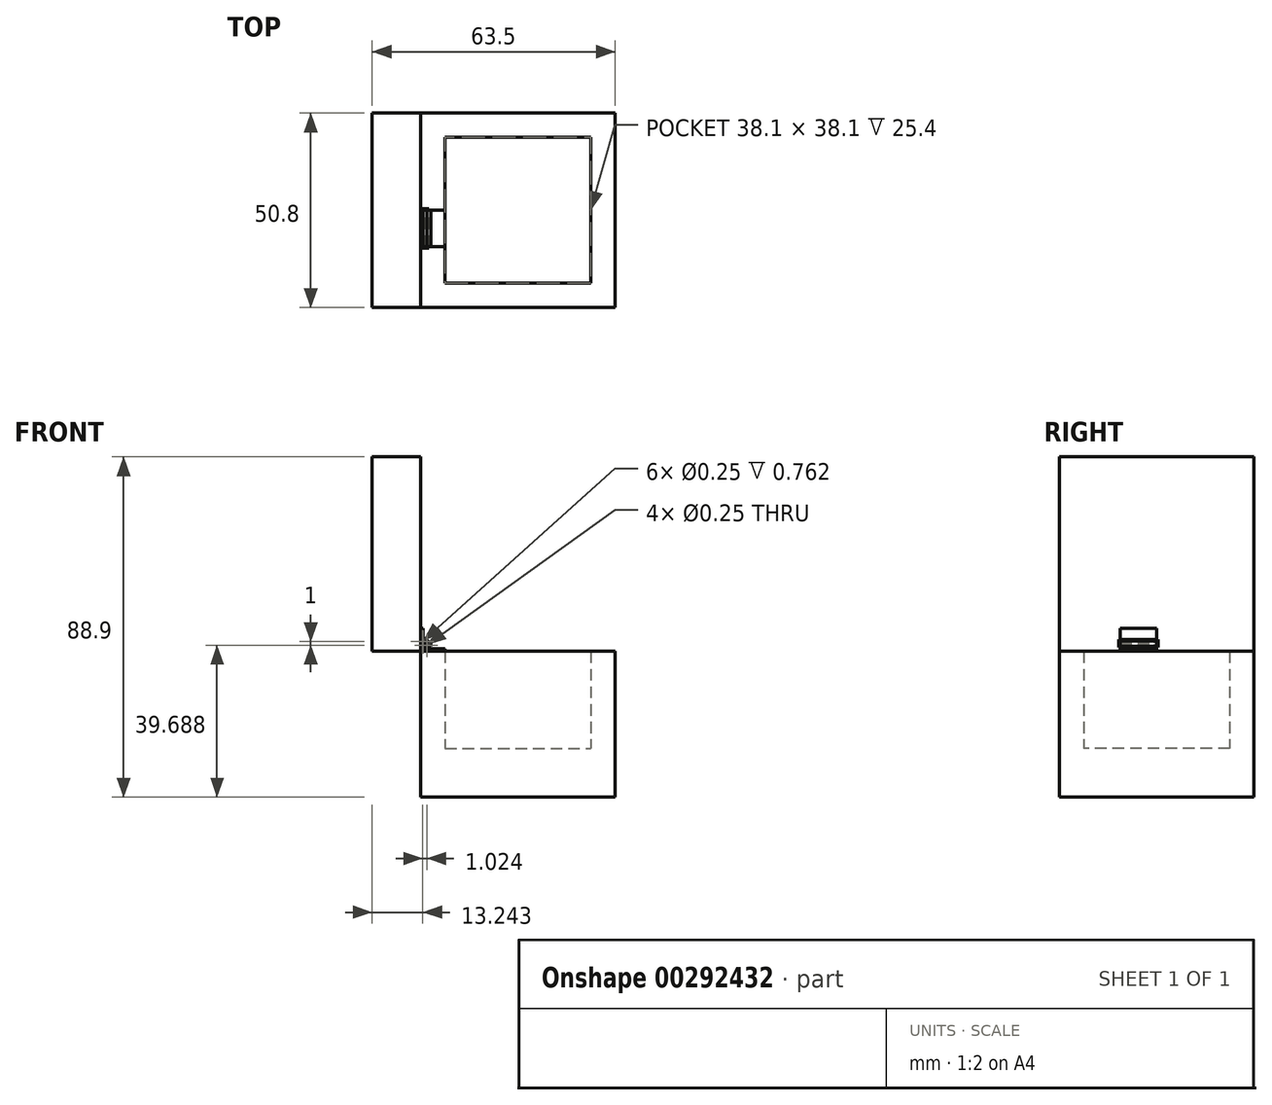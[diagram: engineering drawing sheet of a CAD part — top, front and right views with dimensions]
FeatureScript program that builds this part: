
annotation { "Feature Type Name" : "Feature", "Feature Type Description" : "" }
export const myFeature = defineFeature(function(context is Context, id is Id, definition is map)
    precondition{}
    {
        {
            var Q0;
            Q0=qCreatedBy(makeId("Top.planeOp"),FACE);
            var sketch = newSketch(context, id + "F0", { "sketchPlane" : qUnion([Q0])});
            skLineSegment(sketch, "E0.bottom", {"start": v(0, 25.41) * mm, "end": v(50.8, 25.41) * mm});
            skLineSegment(sketch, "E0.top", {"start": v(0, -25.39) * mm, "end": v(50.8, -25.39) * mm});
            skLineSegment(sketch, "E0.left", {"start": v(0, 25.41) * mm, "end": v(0, -25.39) * mm});
            skLineSegment(sketch, "E0.right", {"start": v(50.8, 25.41) * mm, "end": v(50.8, -25.39) * mm});
            skPoint(sketch, "E0.middle", {"position": v(25.4, 0.01) * mm});
            skLineSegment(sketch, "E1.bottom", {"start": v(6.35, 19.06) * mm, "end": v(44.45, 19.06) * mm});
            skLineSegment(sketch, "E1.top", {"start": v(6.35, -19.04) * mm, "end": v(44.45, -19.04) * mm});
            skLineSegment(sketch, "E1.left", {"start": v(6.35, 19.06) * mm, "end": v(6.35, -19.04) * mm});
            skLineSegment(sketch, "E1.right", {"start": v(44.45, 19.06) * mm, "end": v(44.45, -19.04) * mm});
            skSolve(sketch);
        }
        {
            var Q0;
            Q0=makeQuery(id+"F0.imprint","IMPRINT",FACE,{"disambiguationData":[TD([[makeQuery(id+"F0.imprint","IMPRINT",EDGE,{"derivedFrom":sQuery(id+"F0.wireOp",EDGE,"E0.bottom")}),-1.0]])]});
            extrude(context, id + "F1", {"entities" : qUnion([Q0]), "depth" : 25.4 * mm});
        }
        {
            var Q0;
            Q0=qCreatedBy(makeId("Top.planeOp"),FACE);
            var sketch = newSketch(context, id + "F2", { "sketchPlane" : qUnion([Q0])});
            skLineSegment(sketch, "E2.bottom", {"start": v(50.8, 25.41) * mm, "end": v(0, 25.41) * mm});
            skLineSegment(sketch, "E2.top", {"start": v(50.8, -25.39) * mm, "end": v(0, -25.39) * mm});
            skLineSegment(sketch, "E2.left", {"start": v(50.8, 25.41) * mm, "end": v(50.8, -25.39) * mm});
            skLineSegment(sketch, "E2.right", {"start": v(0, 25.41) * mm, "end": v(0, -25.39) * mm});
            skPoint(sketch, "E2.middle", {"position": v(25.4, 0.01) * mm});
            skSolve(sketch);
        }
        {
            var Q0;
            Q0=makeQuery(id+"F2.imprint","IMPRINT",FACE,{"disambiguationData":[TD([[makeQuery(id+"F2.imprint","IMPRINT",EDGE,{"derivedFrom":sQuery(id+"F2.wireOp",EDGE,"E2.bottom")}),1.0]])]});
            extrude(context, id + "F3", {"entities" : qUnion([Q0]), "operationType" : NewBodyOperationType.ADD, "oppositeDirection" : true, "depth" : 12.7 * mm});
        }
        {
            var Q0;
            Q0=qCreatedBy(makeId("Right.planeOp"),FACE);
            var sketch = newSketch(context, id + "F4", { "sketchPlane" : qUnion([Q0])});
            skLineSegment(sketch, "E3.bottom", {"start": v(25.41, 25.4) * mm, "end": v(-25.39, 25.4) * mm});
            skLineSegment(sketch, "E3.top", {"start": v(25.41, 38.1) * mm, "end": v(-25.39, 38.1) * mm});
            skLineSegment(sketch, "E3.left", {"start": v(25.41, 25.4) * mm, "end": v(25.41, 38.1) * mm});
            skLineSegment(sketch, "E3.right", {"start": v(-25.39, 25.4) * mm, "end": v(-25.39, 38.1) * mm});
            skSolve(sketch);
        }
        {
            var Q0;
            Q0=qSketchRegion(id+"F4",true);
            extrude(context, id + "F5", {"entities" : qUnion([Q0]), "depth" : 50.8 * mm});
        }
        {
            var Q0;
            Q0=makeQuery(id+"F5.opExtrude","SWEPT_BODY",BODY,{"disambiguationData":[OSD([sQuery(id+"F4.wireOp",EDGE,"E3.bottom"),sQuery(id+"F4.wireOp",EDGE,"E3.top"),sQuery(id+"F4.wireOp",EDGE,"E3.left"),sQuery(id+"F4.wireOp",EDGE,"E3.right")])]});
            var Q1;
            Q1=makeQuery(id+"F5.opExtrude","CAP_EDGE",EDGE,{"disambiguationData":[OSD([sQuery(id+"F4.wireOp",EDGE,"E3.bottom")])],"isStart":true});
            transform(context, id + "F6", {"entities" : qUnion([Q0]), "transformType" : TransformType.ROTATION, "transformAxis" : qUnion([Q1]), "angle" : 90 * degree, "makeCopy" : false});
        }
        {
            var Q0;
            Q0=qCreatedBy(makeId("Front.planeOp"),FACE);
            var sketch = newSketch(context, id + "F7", { "sketchPlane" : qUnion([Q0])});
            skLineSegment(sketch, "E4.bottom", {"start": v(6.35, 26.04) * mm, "end": v(2.54, 26.04) * mm});
            skLineSegment(sketch, "E4.top", {"start": v(6.35, 25.4) * mm, "end": v(2.54, 25.4) * mm});
            skLineSegment(sketch, "E4.left", {"start": v(6.35, 26.04) * mm, "end": v(6.35, 25.4) * mm});
            skLineSegment(sketch, "E5", {"start": v(2.54, 26.04) * mm, "end": v(2.54, 25.4) * mm});
            skPoint(sketch, "E6", {"position": v(2.54, 26.04) * mm});
            skLineSegment(sketch, "E7", {"start": v(2.54, 26.04) * mm, "end": v(1.59, 26.48) * mm});
            skArc(sketch, "E8", {"start": v(2.07, 27.09) * mm, "mid": v(1.17, 27.3) * mm, "end": v(1.59, 26.48) * mm});
            skPoint(sketch, "E9", {"position": v(1.56, 25.85) * mm});
            skLineSegment(sketch, "E10", {"start": v(2.54, 25.4) * mm, "end": v(1.56, 25.85) * mm});
            skArc(sketch, "E11", {"start": v(2.7, 26.99) * mm, "mid": v(0.77, 27.8) * mm, "end": v(1.56, 25.85) * mm});
            skLineSegment(sketch, "E12", {"start": v(2.7, 26.99) * mm, "end": v(2.7, 26.76) * mm});
            skLineSegment(sketch, "E13", {"start": v(2.07, 27.09) * mm, "end": v(2.09, 26.98) * mm});
            skLineSegment(sketch, "E14", {"start": v(2.7, 26.76) * mm, "end": v(2.09, 26.98) * mm});
            skPoint(sketch, "E15", {"position": v(6.35, 25.4) * mm});
            skPoint(sketch, "E16", {"position": v(6.35, 26.04) * mm});
            skSolve(sketch);
        }
        {
            var Q0;
            {var subQ2=sQuery(id+"F7.wireOp",EDGE,"49d8aea8-701a-44cc-aa5f-3c914806f390");Q0=makeQuery(id+"F7.imprint","IMPRINT",FACE,{"disambiguationData":[TD([[makeQuery(id+"F7.imprint","IMPRINT",EDGE,{"derivedFrom":subQ2}),1.0]])]});}
            var Q1;
            Q1=makeQuery(id+"F7.imprint","IMPRINT",FACE,{"disambiguationData":[TD([[makeQuery(id+"F7.imprint","IMPRINT",EDGE,{"derivedFrom":sQuery(id+"F7.wireOp",EDGE,"453310b4-ccfe-4605-a67d-a863b6ff2596")}),-1.0]])]});
            var Q2;
            Q2=makeQuery(id+"F7.imprint","IMPRINT",FACE,{"disambiguationData":[TD([[makeQuery(id+"F7.imprint","IMPRINT",EDGE,{"derivedFrom":sQuery(id+"F7.wireOp",EDGE,"E4.bottom")}),1.0]])]});
            extrude(context, id + "F8", {"entities" : qUnion([Q0, Q1, Q2]), "operationType" : NewBodyOperationType.ADD, "depth" : 9.52 * mm});
        }
        {
            var Q0;
            Q0=qCreatedBy(makeId("Front.planeOp"),FACE);
            var sketch = newSketch(context, id + "F9", { "sketchPlane" : qUnion([Q0])});
            skPoint(sketch, "E17", {"position": v(1.57, 28.12) * mm});
            skPoint(sketch, "E18", {"position": v(0.96, 27.94) * mm});
            skPoint(sketch, "E19", {"position": v(0.64, 28.5) * mm});
            skLineSegment(sketch, "E20", {"start": v(0, 28.27) * mm, "end": v(0, 27.63) * mm});
            skPoint(sketch, "E21.MirrorP", {"position": v(0.64, 27.63) * mm});
            skLineSegment(sketch, "E22.MirrorCS", {"start": v(0.64, 31.44) * mm, "end": v(0, 31.44) * mm});
            skLineSegment(sketch, "E23", {"start": v(0, 31.44) * mm, "end": v(0, 28.27) * mm});
            skPoint(sketch, "E24", {"position": v(0.8, 27.82) * mm});
            skLineSegment(sketch, "E25", {"start": v(0.64, 31.44) * mm, "end": v(0.64, 28.5) * mm});
            skLineSegment(sketch, "E26", {"start": v(1.57, 28.12) * mm, "end": v(1.57, 28.5) * mm});
            skLineSegment(sketch, "E27", {"start": v(1.57, 28.5) * mm, "end": v(0.64, 28.5) * mm});
            skArc(sketch, "E28", {"start": v(1.57, 28.12) * mm, "mid": v(1.04, 28) * mm, "end": v(0.64, 27.63) * mm});
            skPoint(sketch, "E29", {"position": v(1.57, 26.99) * mm});
            skCircle(sketch, "E30", {"center": v(1.57, 26.99) * mm, "radius": 0.5 * mm});
            skPoint(sketch, "E31", {"position": v(0.5, 27.37) * mm});
            skArc(sketch, "E32", {"start": v(0.64, 27.63) * mm, "mid": v(0.48, 27.33) * mm, "end": v(0.43, 26.99) * mm});
            skLineSegment(sketch, "E33", {"start": v(0.43, 26.99) * mm, "end": v(0, 26.99) * mm});
            skLineSegment(sketch, "E34", {"start": v(0, 27.63) * mm, "end": v(0, 26.99) * mm});
            skSolve(sketch);
        }
        {
            var Q0;
            Q0=qSketchRegion(id+"F7",true);
            extrude(context, id + "F10", {"entities" : qUnion([Q0]), "operationType" : NewBodyOperationType.ADD, "depth" : 9.52 * mm});
        }
        {
            var Q0;
            {var subQ0=sQuery(id+"F9.wireOp",EDGE,"E30");var subQ1=makeQuery(id+"F9.imprint","INTERSECT",VERTEX,{"derivedFrom":[subQ0,sQuery(id+"F9.wireOp",EDGE,"qVxJkQmu-DeZt-bHWC-hwNS-qI8DtV47FeaQ")]});Q0=makeQuery(id+"F9.imprint","IMPRINT",FACE,{"disambiguationData":[TD([[makeQuery(id+"F9.imprint","IMPRINT",EDGE,{"disambiguationData":[TD([[subQ1,-1.0]])],"derivedFrom":subQ0}),1.0]])]});}
            var Q1;
            Q1=makeQuery(id+"F9.imprint","IMPRINT",FACE,{"disambiguationData":[TD([[makeQuery(id+"F9.imprint","IMPRINT",EDGE,{"derivedFrom":sQuery(id+"F9.wireOp",EDGE,"E20")}),1.0]])]});
            extrude(context, id + "F11", {"entities" : qUnion([Q0, Q1]), "depth" : 9.52 * mm});
        }
        {
            var Q0;
            Q0=makeQuery(id+"F9.imprint","IMPRINT",FACE,{"disambiguationData":[TD([[makeQuery(id+"F9.imprint","IMPRINT",EDGE,{"derivedFrom":sQuery(id+"F9.wireOp",EDGE,"E30")}),1.0]])]});
            extrude(context, id + "F12", {"entities" : qUnion([Q0]), "depth" : 9.52 * mm});
        }
        {
            var Q0;
            Q0=makeQuery(id+"F7.imprint","IMPRINT",FACE,{"disambiguationData":[TD([[makeQuery(id+"F7.imprint","IMPRINT",EDGE,{"derivedFrom":sQuery(id+"F7.wireOp",EDGE,"E5")}),-1.0]])]});
            var sketch = newSketch(context, id + "F13", { "sketchPlane" : qUnion([Q0])});
            skPoint(sketch, "E35", {"position": v(1.57, 26.99) * mm});
            skPoint(sketch, "E36", {"position": v(1.18, 27.31) * mm});
            skPoint(sketch, "E37", {"position": v(1.57, 27.5) * mm});
            skPoint(sketch, "E38", {"position": v(1.06, 26.99) * mm});
            skPoint(sketch, "E39", {"position": v(2, 26.72) * mm});
            skLineSegment(sketch, "E40", {"start": v(1.06, 26.99) * mm, "end": v(1.59, 26.48) * mm});
            skLineSegment(sketch, "E41", {"start": v(1.57, 27.5) * mm, "end": v(2.08, 26.99) * mm});
            skLineSegment(sketch, "E42", {"start": v(1.06, 26.99) * mm, "end": v(0.05, 27.96) * mm});
            skLineSegment(sketch, "E43", {"start": v(1.57, 27.5) * mm, "end": v(0.56, 28.46) * mm});
            skLineSegment(sketch, "E44", {"start": v(0.05, 27.96) * mm, "end": v(0.56, 28.46) * mm});
            skLineSegment(sketch, "E45", {"start": v(1.59, 26.48) * mm, "end": v(2.08, 26.99) * mm});
            skCircle(sketch, "E46", {"center": v(1.57, 26.99) * mm, "radius": 0.13 * mm});
            skCircle(sketch, "E47", {"center": v(0.57, 27.96) * mm, "radius": 0.13 * mm});
            skSolve(sketch);
        }
        {
            var Q0;
            {var subQ0=sQuery(id+"F7.wireOp",EDGE,"E4.left");var subQ1=sQuery(id+"F7.wireOp",EDGE,"E4.top");var subQ2=sQuery(id+"F7.wireOp",EDGE,"E4.bottom");Q0=makeQuery(id+"F10.boolean.opBoolean","MERGE",FACE,{"derivedFrom":[makeQuery(id+"F8.opExtrude","CAP_FACE",FACE,{"disambiguationData":[OSD([subQ2,subQ1,subQ0,sQuery(id+"F7.wireOp",EDGE,"E5")])],"isStart":false}),makeQuery(id+"F10.opExtrude","CAP_FACE",FACE,{"disambiguationData":[OSD([subQ2,subQ1,subQ0,sQuery(id+"F7.wireOp",EDGE,"E7"),sQuery(id+"F7.wireOp",EDGE,"E8"),sQuery(id+"F7.wireOp",EDGE,"E10"),sQuery(id+"F7.wireOp",EDGE,"E11"),sQuery(id+"F7.wireOp",EDGE,"E12"),sQuery(id+"F7.wireOp",EDGE,"E13"),sQuery(id+"F7.wireOp",EDGE,"E14")])],"isStart":false})]});}
            var sketch = newSketch(context, id + "F14", { "sketchPlane" : qUnion([Q0])});
            skPoint(sketch, "E48", {"position": v(1.57, 26.99) * mm});
            skPoint(sketch, "E49", {"position": v(1.18, 27.31) * mm});
            skPoint(sketch, "E50", {"position": v(1.57, 27.5) * mm});
            skPoint(sketch, "E51", {"position": v(1.06, 26.99) * mm});
            skPoint(sketch, "E52", {"position": v(2, 26.72) * mm});
            skLineSegment(sketch, "E53", {"start": v(1.06, 26.99) * mm, "end": v(1.59, 26.48) * mm});
            skLineSegment(sketch, "E54", {"start": v(1.57, 27.5) * mm, "end": v(2.08, 26.99) * mm});
            skLineSegment(sketch, "E55", {"start": v(1.06, 26.99) * mm, "end": v(0.05, 27.96) * mm});
            skLineSegment(sketch, "E56", {"start": v(1.57, 27.5) * mm, "end": v(0.56, 28.46) * mm});
            skLineSegment(sketch, "E57", {"start": v(0.05, 27.96) * mm, "end": v(0.56, 28.46) * mm});
            skLineSegment(sketch, "E58", {"start": v(1.59, 26.48) * mm, "end": v(2.08, 26.99) * mm});
            skCircle(sketch, "E59", {"center": v(0.54, 27.99) * mm, "radius": 0.13 * mm});
            skCircle(sketch, "E60", {"center": v(1.57, 26.99) * mm, "radius": 0.13 * mm});
            skSolve(sketch);
        }
        {
            var Q0;
            Q0=qSketchRegion(id+"F13",true);
            extrude(context, id + "F15", {"entities" : qUnion([Q0]), "oppositeDirection" : true, "depth" : 0.38 * mm});
        }
        {
            var Q0;
            Q0=qSketchRegion(id+"F14",true);
            extrude(context, id + "F16", {"entities" : qUnion([Q0]), "depth" : 0.38 * mm});
        }
        {
            var Q0;
            Q0=makeQuery(id+"F13.imprint","IMPRINT",FACE,{"disambiguationData":[TD([[makeQuery(id+"F13.imprint","IMPRINT",EDGE,{"derivedFrom":sQuery(id+"F13.wireOp",EDGE,"E46")}),1.0]])]});
            var Q1;
            Q1=makeQuery(id+"F13.imprint","IMPRINT",FACE,{"disambiguationData":[TD([[makeQuery(id+"F13.imprint","IMPRINT",EDGE,{"derivedFrom":sQuery(id+"F13.wireOp",EDGE,"E47")}),1.0]])]});
            extrude(context, id + "F17", {"entities" : qUnion([Q0, Q1]), "operationType" : NewBodyOperationType.REMOVE, "depth" : 0.76 * mm});
        }
        {
            var Q0;
            Q0=makeQuery(id+"F14.imprint","IMPRINT",FACE,{"disambiguationData":[TD([[makeQuery(id+"F14.imprint","IMPRINT",EDGE,{"derivedFrom":sQuery(id+"F14.wireOp",EDGE,"E60")}),1.0]])]});
            var Q1;
            Q1=makeQuery(id+"F14.imprint","IMPRINT",FACE,{"disambiguationData":[TD([[makeQuery(id+"F14.imprint","IMPRINT",EDGE,{"derivedFrom":sQuery(id+"F14.wireOp",EDGE,"E59")}),1.0]])]});
            extrude(context, id + "F18", {"entities" : qUnion([Q0, Q1]), "operationType" : NewBodyOperationType.REMOVE, "oppositeDirection" : true, "depth" : 0.76 * mm});
        }
    });
